# Revit family: Pump_Commercial-Submersible-Zoeller-280_Automatic_Series
name_source: partatom
category: Mechanical Equipment
revit_build: Autodesk Revit 2014 (Build: 20130308_1515(x64)
units: mm (PartAtom-declared; Revit-internal decimal feet)

## types (5) — shared parameters
Assembly Code = D2090
Auto On/Off Points = 16-1/2" (40.6 cm) / 5-1/4" (13 cm)
Cooling = Oil Filled
Cord Length = 120"
Cord Type = 1 Ph-UL listed 3-wire neoprene cord and plug
Default Elevation = 0"
Description = Single Seal Automatic Submersible Sewage or Dewatering Pumps
Discharge Diameter = 2"
Discharge Height = 6 1/4"
Discharge Radius = 1"
Gasket = Neoprene square ring and gasket
Hardware = Stainless steel
Height = 19 9/16"
Hertz = 60
Impeller = Cast Iron
Impeller Type = Non-clogging vortex
Installation Type = Floor Mounted
Insulation = Class B
Length = 13 9/16"
Lower Bearing = Ball Bearing
Manufacturer = Zoeller
Material = Cast Iron-Zoeller-Powder Coated Epoxy
Max. Operating Temp. = 130.00 °F
Mechanical Seals = Carbon and Ceramic
Motor Protection = Auto reset thermal overload (1 Ph)
Motor Shaft = 1117 carbon steel
Operation = Automatic
Phase = 1
Price = Prices may vary. Please consult Manufacturer Representative for most up-to-date price list.
Product Documentation Link = http://cdn.qleapahead.com
Product Page URL = http://www.zoellerpumps.com
RPM = 1725
Solid Handling = 2" Spherical Solids
Type = Permanent Split Capacitor
Type Comments = Available in single or double seal designs.
URL = http://www.zoellerpumps.com
Upper Bearing = Ball Bearing
Warranty Information = 36 Months (Limited)
Waste Connection = Yes
Width = 10"

## per-type parameters (varying)
| type | Amps | Apparent Load | Flow @ 5' | Max. Head | Model | Motor | Shipping Weight | Voltage |
| M282 - 115V/1Ph/10.3A/0.5HP | 10 A | 1185 VA | 127 GPM | 26' (7.9 m) | M282 | 1/2 HP | 82 lbs | 115 V |
| D282 - 230V/1Ph/5A/0.5HP | 5 A | 1150 VA | 127 GPM | 26' (7.9 m) | D282 | 1/2 HP | 82 lbs | 230 V |
| H282 - 200V/1Ph/6.1A/0.5HP | 6 A | 1220 VA | 127 GPM | 26' (7.9 m) | H282 | 1/2 HP | 82 lbs | 200 V |
| D284 - 230V/1Ph/8.9A/1HP | 9 A | 2047 VA | 179 GPM | 35' (10.7 m) | D284 | 1 HP | 85 lbs | 230 V |
| H284 - 200V/1Ph/9.3A/1HP | 9 A | 1860 VA | 179 GPM | 35' (10.7 m) | H284 | 1 HP | 85 lbs | 200 V |

## geometry (parser evidence)
native form markers: Sweep x3
no freeform markers — native parametric forms only
